# Revit family: Sanitary_Other-Sanitary_hansgrohe_50001XXX-hansgrohe-Waste-set-non-closing__NEW
name_source: partatom
category: Furniture
revit_build: Autodesk Revit 2015 (Build: 20140903_1530(x64)
units: mm (PartAtom-declared; Revit-internal decimal feet)

## types (2) — shared parameters
Always visible = Yes
BIMobject category = Other Sanitary
BIMobject category code = sanitary-sanitary-other
BIMobject main category = Sanitary
BIMobject main category code = sanitary
Brand url = http://www.hansgrohe-int.com
Design country = Germany
Edition number = 1
GTIN code = https://4011097146867
IFC Classification = Sanitary Terminal
Installation instructions = https://www.hansgrohe.com
Manufacturer country = Germany
Manufacturer name = hansgrohe
Material 2 = Hansgrohe - Hansgrohe - Black
Material main = Brass
Material secondary = Chrome
Product Guid = 01815c31-8efc-49bb-ac8f-1bd6fda3c5a5
Product SKU = 50001XXX
Product data url = https://bimobject.com
Product family = hansgrohe
Product group = Waste systems washbasin
Product name = 50001XXX hansgrohe Waste set non-closing for washbasins
Product url = https://www.hansgrohe.com
QR code = http://bimobject.com
Technical description = https://www.hansgrohe.com

## per-type parameters (varying)
| type | Material 1 |
| 700 Matt White | Hansgrohe - Hansgrohe - 700 Matt White |
| 670 Matte Black | Hansgrohe - Hansgrohe - 670 Matte Black |

## geometry (parser evidence)
native form markers: Sweep x3
no freeform markers — native parametric forms only
